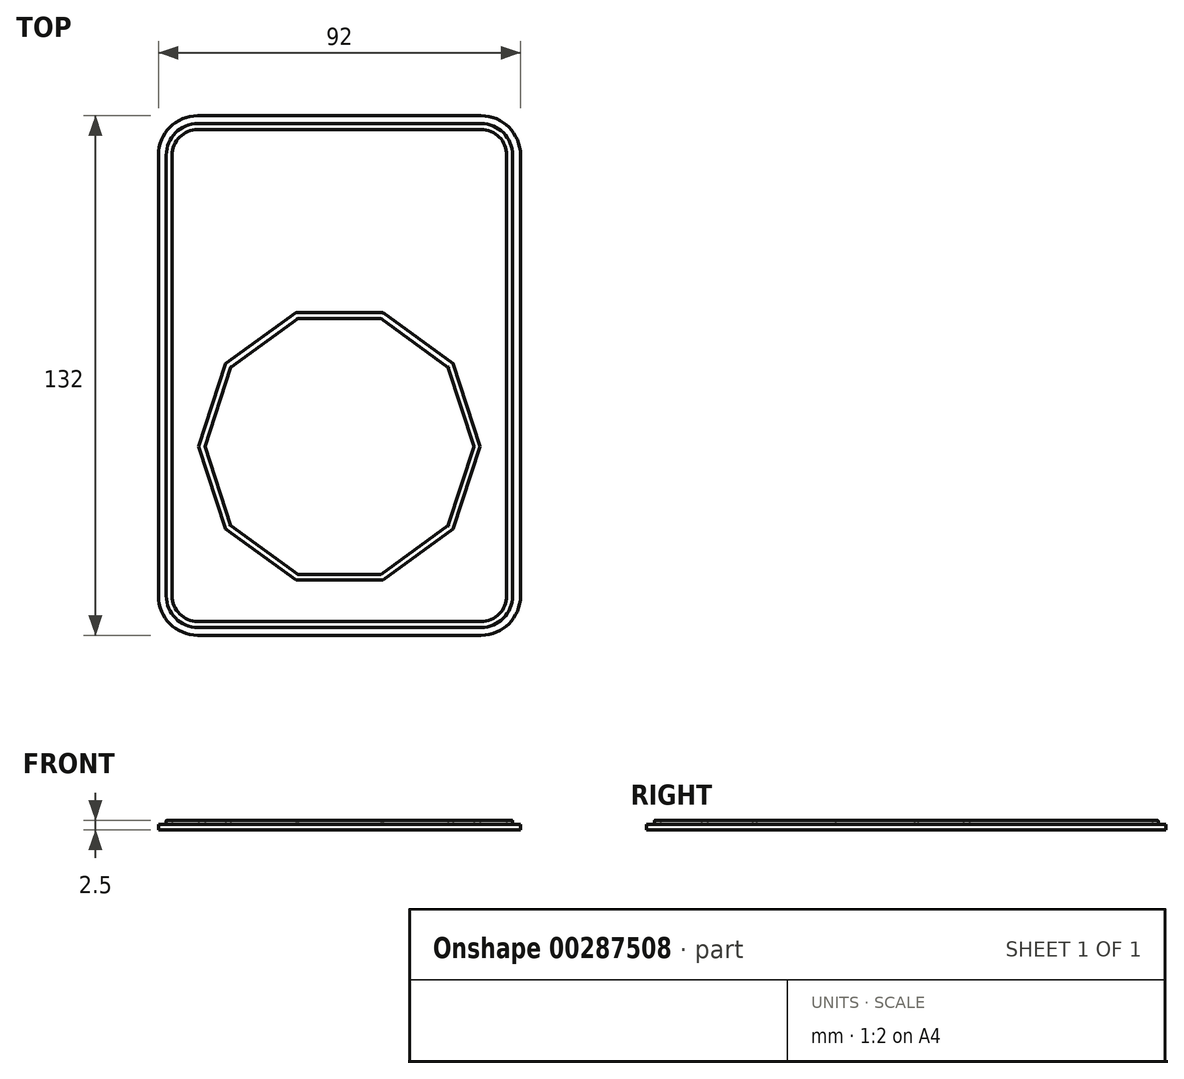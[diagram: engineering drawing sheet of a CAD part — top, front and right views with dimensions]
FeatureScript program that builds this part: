
annotation { "Feature Type Name" : "Feature", "Feature Type Description" : "" }
export const myFeature = defineFeature(function(context is Context, id is Id, definition is map)
    precondition{}
    {
        {
            var Q0;
            Q0=qCreatedBy(makeId("Top.planeOp"),FACE);
            var sketch = newSketch(context, id + "F0", { "sketchPlane" : qUnion([Q0])});
            skLineSegment(sketch, "E0.bottom", {"start": v(-36, 137.93) * mm, "end": v(36, 137.93) * mm});
            skLineSegment(sketch, "E0.top", {"start": v(-36, 5.93) * mm, "end": v(36, 5.93) * mm});
            skLineSegment(sketch, "E0.left", {"start": v(-46, 127.93) * mm, "end": v(-46, 15.93) * mm});
            skLineSegment(sketch, "E0.right", {"start": v(46, 127.93) * mm, "end": v(46, 15.93) * mm});
            skPoint(sketch, "E1.visualSharp", {"position": v(46, 5.93) * mm});
            skArc(sketch, "E1.filletArc", {"start": v(36, 5.93) * mm, "mid": v(43.07, 8.86) * mm, "end": v(46, 15.93) * mm});
            skPoint(sketch, "E2.visualSharp", {"position": v(-46, 5.93) * mm});
            skArc(sketch, "E2.filletArc", {"start": v(-46, 15.93) * mm, "mid": v(-43.07, 8.86) * mm, "end": v(-36, 5.93) * mm});
            skPoint(sketch, "E3.visualSharp", {"position": v(-46, 137.93) * mm});
            skArc(sketch, "E3.filletArc", {"start": v(-36, 137.93) * mm, "mid": v(-43.07, 135) * mm, "end": v(-46, 127.93) * mm});
            skPoint(sketch, "E4.visualSharp", {"position": v(46, 137.93) * mm});
            skArc(sketch, "E4.filletArc", {"start": v(46, 127.93) * mm, "mid": v(43.07, 135) * mm, "end": v(36, 137.93) * mm});
            skLineSegment(sketch, "E5.0", {"start": v(-44, 127.93) * mm, "end": v(-44, 15.93) * mm, "construction": true});
            skArc(sketch, "E5.1", {"start": v(-36, 135.93) * mm, "mid": v(-41.66, 133.6) * mm, "end": v(-44, 127.93) * mm, "construction": true});
            skArc(sketch, "E5.2", {"start": v(-44, 15.93) * mm, "mid": v(-41.66, 10.28) * mm, "end": v(-36, 7.93) * mm, "construction": true});
            skLineSegment(sketch, "E5.3", {"start": v(-36, 135.93) * mm, "end": v(36, 135.93) * mm, "construction": true});
            skLineSegment(sketch, "E5.4", {"start": v(-36, 7.93) * mm, "end": v(36, 7.93) * mm, "construction": true});
            skArc(sketch, "E5.5", {"start": v(36, 7.93) * mm, "mid": v(41.66, 10.28) * mm, "end": v(44, 15.93) * mm, "construction": true});
            skLineSegment(sketch, "E5.6", {"start": v(44, 127.93) * mm, "end": v(44, 15.93) * mm, "construction": true});
            skArc(sketch, "E5.7", {"start": v(44, 127.93) * mm, "mid": v(41.66, 133.6) * mm, "end": v(36, 135.93) * mm, "construction": true});
            skLineSegment(sketch, "E6", {"start": v(-46, 71.93) * mm, "end": v(28.74, 71.93) * mm});
            skSolve(sketch);
        }
        {
            var Q0;
            Q0=qCreatedBy(makeId("Top.planeOp"),FACE);
            var sketch = newSketch(context, id + "F1", { "sketchPlane" : qUnion([Q0])});
            skCircle(sketch, "E7.cCircle", {"center": v(0, 53.93) * mm, "radius": 32.5 * mm, "construction": true});
            skLineSegment(sketch, "E7.0", {"start": v(10.56, 86.43) * mm, "end": v(27.65, 74.02) * mm});
            skLineSegment(sketch, "E7.1", {"start": v(27.65, 74.02) * mm, "end": v(34.17, 53.93) * mm});
            skLineSegment(sketch, "E7.2", {"start": v(34.17, 53.93) * mm, "end": v(27.65, 33.85) * mm});
            skLineSegment(sketch, "E7.3", {"start": v(27.65, 33.85) * mm, "end": v(10.56, 21.43) * mm});
            skLineSegment(sketch, "E7.4", {"start": v(10.56, 21.43) * mm, "end": v(-10.56, 21.43) * mm});
            skLineSegment(sketch, "E7.5", {"start": v(-10.56, 21.43) * mm, "end": v(-27.65, 33.85) * mm});
            skLineSegment(sketch, "E7.6", {"start": v(-27.65, 33.85) * mm, "end": v(-34.17, 53.93) * mm});
            skLineSegment(sketch, "E7.7", {"start": v(-34.17, 53.93) * mm, "end": v(-27.65, 74.02) * mm});
            skLineSegment(sketch, "E7.8", {"start": v(-27.65, 74.02) * mm, "end": v(-10.56, 86.43) * mm});
            skLineSegment(sketch, "E7.9", {"start": v(-10.56, 86.43) * mm, "end": v(10.56, 86.43) * mm});
            skPoint(sketch, "E7.0.midPoint", {"position": v(19.1, 80.23) * mm});
            skLineSegment(sketch, "E8", {"start": v(0, 53.93) * mm, "end": v(77.2, 53.93) * mm, "construction": true});
            skLineSegment(sketch, "E9.0", {"start": v(-28.92, 74.95) * mm, "end": v(-11.05, 87.93) * mm});
            skLineSegment(sketch, "E9.1", {"start": v(-35.75, 53.93) * mm, "end": v(-28.92, 74.95) * mm});
            skLineSegment(sketch, "E9.2", {"start": v(-11.05, 87.93) * mm, "end": v(11.05, 87.93) * mm});
            skLineSegment(sketch, "E9.3", {"start": v(-28.92, 32.92) * mm, "end": v(-35.75, 53.93) * mm});
            skLineSegment(sketch, "E9.4", {"start": v(-11.05, 19.93) * mm, "end": v(-28.92, 32.92) * mm});
            skLineSegment(sketch, "E9.5", {"start": v(11.05, 19.93) * mm, "end": v(-11.05, 19.93) * mm});
            skLineSegment(sketch, "E9.6", {"start": v(11.05, 87.93) * mm, "end": v(28.92, 74.95) * mm});
            skLineSegment(sketch, "E9.7", {"start": v(28.92, 74.95) * mm, "end": v(35.75, 53.93) * mm});
            skLineSegment(sketch, "E9.8", {"start": v(35.75, 53.93) * mm, "end": v(28.92, 32.92) * mm});
            skLineSegment(sketch, "E9.9", {"start": v(28.92, 32.92) * mm, "end": v(11.05, 19.93) * mm});
            skSolve(sketch);
        }
        {
            var Q0;
            Q0=qCreatedBy(makeId("Top.planeOp"),FACE);
            var sketch = newSketch(context, id + "F2", { "sketchPlane" : qUnion([Q0])});
            skArc(sketch, "E10.0", {"start": v(-36, 135.93) * mm, "mid": v(-41.66, 133.6) * mm, "end": v(-44, 127.93) * mm});
            skLineSegment(sketch, "E10.1", {"start": v(-36, 135.93) * mm, "end": v(36, 135.93) * mm});
            skArc(sketch, "E10.2", {"start": v(44, 127.93) * mm, "mid": v(41.66, 133.6) * mm, "end": v(36, 135.93) * mm});
            skLineSegment(sketch, "E10.3", {"start": v(44, 127.93) * mm, "end": v(44, 15.93) * mm});
            skArc(sketch, "E10.4", {"start": v(36, 7.93) * mm, "mid": v(41.66, 10.28) * mm, "end": v(44, 15.93) * mm});
            skLineSegment(sketch, "E10.5", {"start": v(-36, 7.93) * mm, "end": v(36, 7.93) * mm});
            skArc(sketch, "E10.6", {"start": v(-44, 15.93) * mm, "mid": v(-41.66, 10.28) * mm, "end": v(-36, 7.93) * mm});
            skLineSegment(sketch, "E10.7", {"start": v(-44, 127.93) * mm, "end": v(-44, 15.93) * mm});
            skLineSegment(sketch, "E11.0", {"start": v(-36, 134.43) * mm, "end": v(36, 134.43) * mm});
            skArc(sketch, "E11.1", {"start": v(42.5, 127.93) * mm, "mid": v(40.6, 132.53) * mm, "end": v(36, 134.43) * mm});
            skArc(sketch, "E11.2", {"start": v(-36, 134.43) * mm, "mid": v(-40.6, 132.53) * mm, "end": v(-42.5, 127.93) * mm});
            skLineSegment(sketch, "E11.3", {"start": v(42.5, 127.93) * mm, "end": v(42.5, 15.93) * mm});
            skLineSegment(sketch, "E11.4", {"start": v(-42.5, 127.93) * mm, "end": v(-42.5, 15.93) * mm});
            skArc(sketch, "E11.5", {"start": v(-42.5, 15.93) * mm, "mid": v(-40.6, 11.34) * mm, "end": v(-36, 9.43) * mm});
            skLineSegment(sketch, "E11.6", {"start": v(-36, 9.43) * mm, "end": v(36, 9.43) * mm});
            skArc(sketch, "E11.7", {"start": v(36, 9.43) * mm, "mid": v(40.6, 11.34) * mm, "end": v(42.5, 15.93) * mm});
            skSolve(sketch);
        }
        {
            var Q0;
            Q0 = qSketchRegion(id + "F1", true);
            var Q1;
            Q1 = qSketchRegion(id + "F2", true);
            extrude(context, id + "F3", {"entities" : qUnion([Q0, Q1]), "depth" : 1 * mm});
        }
        {
            var Q0;
            Q0=makeQuery(id+"F3.opExtrude","CAP_FACE",FACE,{"disambiguationData":[OSD([sQuery(id+"F2.wireOp",EDGE,"E10.0"),sQuery(id+"F2.wireOp",EDGE,"E10.1"),sQuery(id+"F2.wireOp",EDGE,"E10.2"),sQuery(id+"F2.wireOp",EDGE,"E10.3"),sQuery(id+"F2.wireOp",EDGE,"E10.4"),sQuery(id+"F2.wireOp",EDGE,"E10.5"),sQuery(id+"F2.wireOp",EDGE,"E10.6"),sQuery(id+"F2.wireOp",EDGE,"E10.7"),sQuery(id+"F2.wireOp",EDGE,"E11.0"),sQuery(id+"F2.wireOp",EDGE,"E11.1"),sQuery(id+"F2.wireOp",EDGE,"E11.2"),sQuery(id+"F2.wireOp",EDGE,"E11.3"),sQuery(id+"F2.wireOp",EDGE,"E11.4"),sQuery(id+"F2.wireOp",EDGE,"E11.5"),sQuery(id+"F2.wireOp",EDGE,"E11.6"),sQuery(id+"F2.wireOp",EDGE,"E11.7")])],"isStart":false});
            var Q1;
            Q1=makeQuery(id+"F3.opExtrude","CAP_FACE",FACE,{"disambiguationData":[OSD([sQuery(id+"F1.wireOp",EDGE,"E7.0"),sQuery(id+"F1.wireOp",EDGE,"E7.1"),sQuery(id+"F1.wireOp",EDGE,"E7.2"),sQuery(id+"F1.wireOp",EDGE,"E7.3"),sQuery(id+"F1.wireOp",EDGE,"E7.4"),sQuery(id+"F1.wireOp",EDGE,"E7.5"),sQuery(id+"F1.wireOp",EDGE,"E7.6"),sQuery(id+"F1.wireOp",EDGE,"E7.7"),sQuery(id+"F1.wireOp",EDGE,"E7.8"),sQuery(id+"F1.wireOp",EDGE,"E7.9"),sQuery(id+"F1.wireOp",EDGE,"E9.0"),sQuery(id+"F1.wireOp",EDGE,"E9.1"),sQuery(id+"F1.wireOp",EDGE,"E9.2"),sQuery(id+"F1.wireOp",EDGE,"E9.3"),sQuery(id+"F1.wireOp",EDGE,"E9.4"),sQuery(id+"F1.wireOp",EDGE,"E9.5"),sQuery(id+"F1.wireOp",EDGE,"E9.6"),sQuery(id+"F1.wireOp",EDGE,"E9.7"),sQuery(id+"F1.wireOp",EDGE,"E9.8"),sQuery(id+"F1.wireOp",EDGE,"E9.9")])],"isStart":false});
            fillet(context, id + "F4", {"entities" : qUnion([Q0, Q1]), "radius" : .2 * mm, "tangentPropagation" : true, "allowEdgeOverflow" : false});
        }
        {
            var Q0;
            Q0=qCreatedBy(makeId("Top.planeOp"),FACE);
            var sketch = newSketch(context, id + "F5", { "sketchPlane" : qUnion([Q0])});
            skCircle(sketch, "E12.cCircle", {"center": v(0, 53.93) * mm, "radius": 42.32 * mm, "construction": true});
            skLineSegment(sketch, "E12.0", {"start": v(26.16, 89.93) * mm, "end": v(42.32, 67.68) * mm});
            skLineSegment(sketch, "E12.1", {"start": v(42.32, 67.68) * mm, "end": v(42.32, 40.18) * mm});
            skLineSegment(sketch, "E12.2", {"start": v(42.32, 40.18) * mm, "end": v(26.16, 17.93) * mm});
            skLineSegment(sketch, "E12.3", {"start": v(26.16, 17.93) * mm, "end": v(0, 9.43) * mm});
            skLineSegment(sketch, "E12.4", {"start": v(0, 9.43) * mm, "end": v(-26.16, 17.93) * mm});
            skLineSegment(sketch, "E12.5", {"start": v(-26.16, 17.93) * mm, "end": v(-42.32, 40.18) * mm});
            skLineSegment(sketch, "E12.6", {"start": v(-42.32, 40.18) * mm, "end": v(-42.32, 67.68) * mm});
            skLineSegment(sketch, "E12.7", {"start": v(-42.32, 67.68) * mm, "end": v(-26.16, 89.93) * mm});
            skLineSegment(sketch, "E12.8", {"start": v(-26.16, 89.93) * mm, "end": v(0, 98.43) * mm});
            skLineSegment(sketch, "E12.9", {"start": v(0, 98.43) * mm, "end": v(26.16, 89.93) * mm});
            skPoint(sketch, "E12.0.midPoint", {"position": v(34.24, 78.8) * mm});
            skSolve(sketch);
        }
        {
            var Q0;
            Q0 = qSketchRegion(id + "F0", true);
            extrude(context, id + "F6", {"entities" : qUnion([Q0]), "oppositeDirection" : true, "depth" : 1.5 * mm});
        }
        {
            var Q0;
            Q0=qCreatedBy(makeId("Top.planeOp"),FACE);
            var sketch = newSketch(context, id + "F7", { "sketchPlane" : qUnion([Q0])});
            skCircle(sketch, "E13.cCircle", {"center": v(0, 53.93) * mm, "radius": 76.56 * mm, "construction": true});
            skLineSegment(sketch, "E13.0", {"start": v(47.32, 119.06) * mm, "end": v(76.56, 78.8) * mm});
            skLineSegment(sketch, "E13.1", {"start": v(76.56, 78.8) * mm, "end": v(76.56, 29.06) * mm});
            skLineSegment(sketch, "E13.2", {"start": v(76.56, 29.06) * mm, "end": v(47.32, -11.2) * mm});
            skLineSegment(sketch, "E13.3", {"start": v(47.32, -11.2) * mm, "end": v(0, -26.57) * mm});
            skLineSegment(sketch, "E13.4", {"start": v(0, -26.57) * mm, "end": v(-47.32, -11.2) * mm});
            skLineSegment(sketch, "E13.5", {"start": v(-47.32, -11.2) * mm, "end": v(-76.56, 29.06) * mm});
            skLineSegment(sketch, "E13.6", {"start": v(-76.56, 29.06) * mm, "end": v(-76.56, 78.8) * mm});
            skLineSegment(sketch, "E13.7", {"start": v(-76.56, 78.8) * mm, "end": v(-47.32, 119.06) * mm});
            skLineSegment(sketch, "E13.8", {"start": v(-47.32, 119.06) * mm, "end": v(0, 134.43) * mm});
            skLineSegment(sketch, "E13.9", {"start": v(0, 134.43) * mm, "end": v(47.32, 119.06) * mm});
            skPoint(sketch, "E13.0.midPoint", {"position": v(61.94, 98.93) * mm});
            skSolve(sketch);
        }
    });
